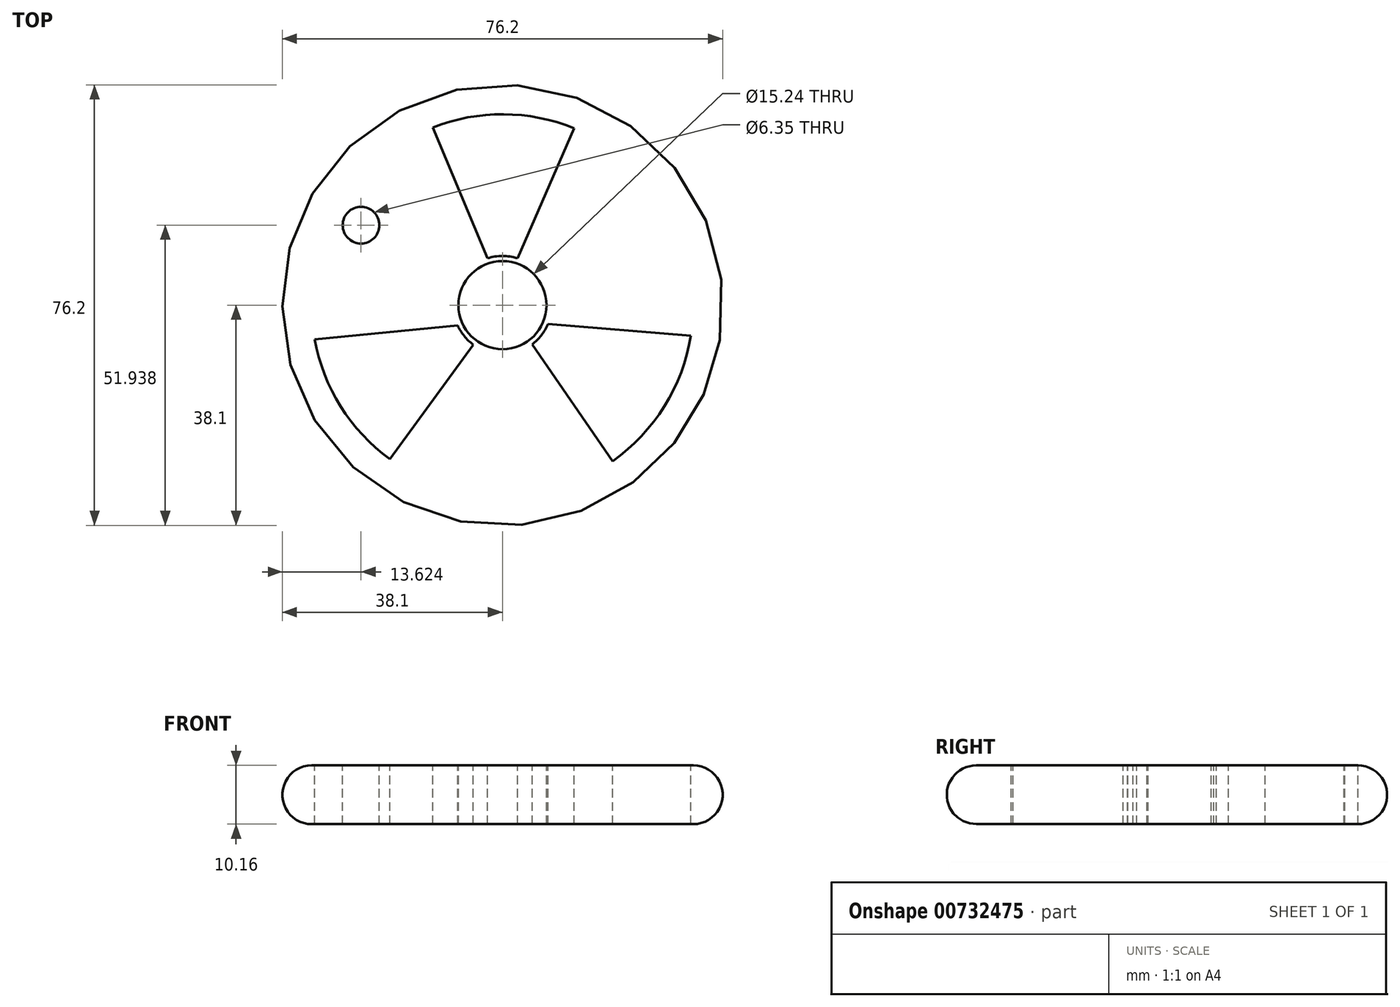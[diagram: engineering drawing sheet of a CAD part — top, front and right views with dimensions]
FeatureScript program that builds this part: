
annotation { "Feature Type Name" : "Feature", "Feature Type Description" : "" }
export const myFeature = defineFeature(function(context is Context, id is Id, definition is map)
    precondition{}
    {
        {
            var Q0;
            Q0=qCreatedBy(makeId("Top.planeOp"),FACE);
            var sketch = newSketch(context, id + "F0", { "sketchPlane" : qUnion([Q0])});
            skCircle(sketch, "E0", {"center": v(0, 0) * mm, "radius": 38.1 * mm});
            skSolve(sketch);
        }
        {
            var Q0;
            Q0=makeQuery(id+"F0.imprint","IMPRINT",FACE,{"disambiguationData":[TD([[makeQuery(id+"F0.imprint","IMPRINT",EDGE,{"derivedFrom":sQuery(id+"F0.wireOp",EDGE,"E0")}),1.0]])]});
            extrude(context, id + "F1", {"entities" : qUnion([Q0]), "depth" : 10.16 * mm, "offsetDistance" : 25.4 * mm});
        }
        {
            var Q0;
            Q0=makeQuery(id+"F1.opExtrude","CAP_EDGE",EDGE,{"disambiguationData":[OSD([sQuery(id+"F0.wireOp",EDGE,"E0")])],"isStart":false});
            var Q1;
            Q1=makeQuery(id+"F1.opExtrude","CAP_EDGE",EDGE,{"disambiguationData":[OSD([sQuery(id+"F0.wireOp",EDGE,"E0")])],"isStart":true});
            fillet(context, id + "F2", {"entities" : qUnion([Q0, Q1]), "radius" : 5.08 * mm, "tangentPropagation" : true, "allowEdgeOverflow" : false});
        }
        {
            var Q0;
            Q0=makeQuery(id+"F1.opExtrude","CAP_FACE",FACE,{"disambiguationData":[OSD([sQuery(id+"F0.wireOp",EDGE,"E0")])],"isStart":false});
            var sketch = newSketch(context, id + "F3", { "sketchPlane" : qUnion([Q0])});
            skCircle(sketch, "E1", {"center": v(0, 0) * mm, "radius": 7.62 * mm});
            skCircle(sketch, "E2", {"center": v(0, 0) * mm, "radius": 8.5 * mm});
            skArc(sketch, "E3", {"start": v(-32.5, -5.89) * mm, "mid": v(-28, -17.51) * mm, "end": v(-19.5, -26.64) * mm});
            skLineSegment(sketch, "E4", {"start": v(2.58, 8.1) * mm, "end": v(12.39, 30.6) * mm});
            skLineSegment(sketch, "E5", {"start": v(-2.58, 8.1) * mm, "end": v(-12.04, 30.75) * mm});
            skLineSegment(sketch, "E6", {"start": v(7.86, -3.25) * mm, "end": v(32.6, -5.26) * mm});
            skLineSegment(sketch, "E7", {"start": v(5.12, -6.8) * mm, "end": v(19.04, -26.98) * mm});
            skLineSegment(sketch, "E8", {"start": v(-7.77, -3.48) * mm, "end": v(-32.5, -5.89) * mm});
            skLineSegment(sketch, "E9", {"start": v(-5.05, -6.85) * mm, "end": v(-19.5, -26.64) * mm});
            skArc(sketch, "E10.trimOffspring", {"start": v(12.39, 30.6) * mm, "mid": v(0.19, 33.02) * mm, "end": v(-12.04, 30.75) * mm});
            skArc(sketch, "E11.trimOffspring", {"start": v(19.04, -26.98) * mm, "mid": v(28, -17.49) * mm, "end": v(32.6, -5.26) * mm});
            skSolve(sketch);
        }
        {
            var Q0;
            Q0=makeQuery(id+"F3.imprint","IMPRINT",FACE,{"disambiguationData":[TD([[makeQuery(id+"F3.imprint","IMPRINT",EDGE,{"derivedFrom":sQuery(id+"F3.wireOp",EDGE,"E1")}),1.0]])]});
            var Q1;
            {var subQ0=sQuery(id+"F3.wireOp",EDGE,"E4");Q1=makeQuery(id+"F3.imprint","IMPRINT",FACE,{"disambiguationData":[TD([[makeQuery(id+"F3.imprint","IMPRINT",EDGE,{"derivedFrom":subQ0}),1.0]])]});}
            var Q2;
            Q2=makeQuery(id+"F3.imprint","IMPRINT",FACE,{"disambiguationData":[TD([[makeQuery(id+"F3.imprint","IMPRINT",EDGE,{"derivedFrom":sQuery(id+"F3.wireOp",EDGE,"E3")}),1.0]])]});
            var Q3;
            {var subQ0=sQuery(id+"F3.wireOp",EDGE,"E6");Q3=makeQuery(id+"F3.imprint","IMPRINT",FACE,{"disambiguationData":[TD([[makeQuery(id+"F3.imprint","IMPRINT",EDGE,{"derivedFrom":subQ0}),-1.0]])]});}
            extrude(context, id + "F4", {"entities" : qUnion([Q0, Q1, Q2, Q3]), "operationType" : NewBodyOperationType.REMOVE, "oppositeDirection" : true, "depth" : 25.4 * mm, "offsetDistance" : 25.4 * mm});
        }
        {
            var Q0;
            Q0=makeQuery(id+"F1.opExtrude","CAP_FACE",FACE,{"disambiguationData":[OSD([sQuery(id+"F0.wireOp",EDGE,"E0")])],"isStart":false});
            var sketch = newSketch(context, id + "F5", { "sketchPlane" : qUnion([Q0])});
            skCircle(sketch, "E12", {"center": v(-24.48, 13.84) * mm, "radius": 3.18 * mm});
            skSolve(sketch);
        }
        {
            var Q0;
            Q0=makeQuery(id+"F5.imprint","IMPRINT",FACE,{"disambiguationData":[TD([[makeQuery(id+"F5.imprint","IMPRINT",EDGE,{"derivedFrom":sQuery(id+"F5.wireOp",EDGE,"E12")}),1.0]])]});
            extrude(context, id + "F6", {"entities" : qUnion([Q0]), "operationType" : NewBodyOperationType.REMOVE, "oppositeDirection" : true, "depth" : 25.4 * mm, "offsetDistance" : 25.4 * mm});
        }
    });
